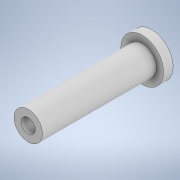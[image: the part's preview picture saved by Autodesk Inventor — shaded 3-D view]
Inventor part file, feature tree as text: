
AUTODESK INVENTOR PART (.ipt)
format: ipt  version: 2020.1 (Build 241239000, 239)  size: 112,128 bytes
history: native  units: mm
features: extrude x3, sketch x3
ambient origin geometry x8: Origin, YZ Plane, XZ Plane, XY Plane, X Axis, Y Axis, Z Axis, Center Point
bodies: Solid1 (feature_tree)
feature tree (6):
  extrude  "Extrusion1"  Depth=4.0mm TaperAngle=0.0deg
  extrude  "Extrusion2"  Depth=6.0mm
  extrude  "Extrusion3"  Depth=27.0mm TaperAngle=0.0deg
  sketch  "Sketch1"  dims[d0=18.0mm d1=4.0mm d2=0.0mm]
  sketch  "Sketch2"  dims[d3=12.0mm d4=6.0mm]
  sketch  "Sketch4"  dims[d5=48.0mm d6=0.0mm d8=27.0mm d9=0.0mm]
